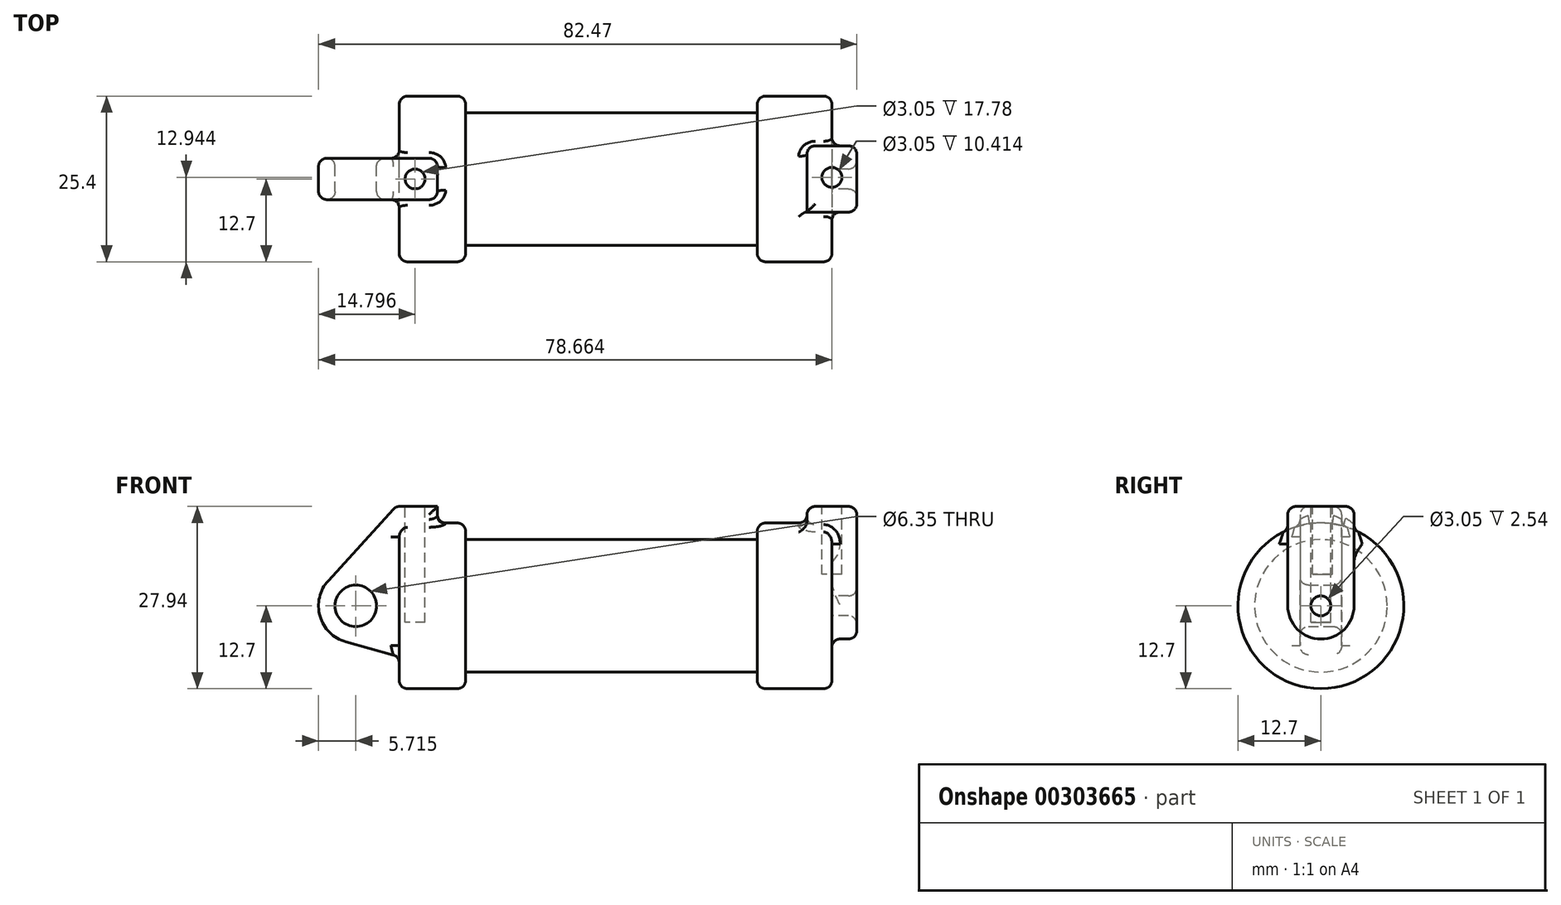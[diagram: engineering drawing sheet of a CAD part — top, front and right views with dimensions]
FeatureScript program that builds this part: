
annotation { "Feature Type Name" : "Feature", "Feature Type Description" : "" }
export const myFeature = defineFeature(function(context is Context, id is Id, definition is map)
    precondition{}
    {
        {
            var Q0;
            Q0=qCreatedBy(makeId("Front.planeOp"),FACE);
            var sketch = newSketch(context, id + "F0", { "sketchPlane" : qUnion([Q0])});
            skLineSegment(sketch, "E0", {"start": v(0, 0) * mm, "end": v(0, 12.7) * mm});
            skLineSegment(sketch, "E1", {"start": v(0, 12.7) * mm, "end": v(10.16, 12.7) * mm});
            skLineSegment(sketch, "E2", {"start": v(10.16, 12.7) * mm, "end": v(10.16, 10.16) * mm});
            skLineSegment(sketch, "E3", {"start": v(10.16, 10.16) * mm, "end": v(56.13, 10.16) * mm});
            skLineSegment(sketch, "E4", {"start": v(56.13, 10.16) * mm, "end": v(56.13, 12.7) * mm});
            skLineSegment(sketch, "E5", {"start": v(56.13, 12.7) * mm, "end": v(66.3, 12.7) * mm});
            skLineSegment(sketch, "E6", {"start": v(66.3, 12.7) * mm, "end": v(66.3, 0) * mm});
            skLineSegment(sketch, "E7", {"start": v(66.3, 0) * mm, "end": v(0, 0) * mm});
            skLineSegment(sketch, "E8", {"start": v(5.84, 15.24) * mm, "end": v(-0.5, 15.24) * mm});
            skLineSegment(sketch, "E9", {"start": v(-0.5, 15.24) * mm, "end": v(-10.88, 3.85) * mm});
            skLineSegment(sketch, "E10", {"start": v(0, 0) * mm, "end": v(-6.65, 0) * mm});
            skCircle(sketch, "E11", {"center": v(-6.65, 0) * mm, "radius": 5.72 * mm});
            skCircle(sketch, "E12", {"center": v(-6.65, 0) * mm, "radius": 3.18 * mm});
            skLineSegment(sketch, "E13", {"start": v(5.84, 15.24) * mm, "end": v(5.84, -9.4) * mm});
            skLineSegment(sketch, "E14", {"start": v(5.84, -9.4) * mm, "end": v(-8.18, -5.5) * mm});
            skCircle(sketch, "E15", {"center": v(-6.65, 0) * mm, "radius": 0.82 * mm});
            skSolve(sketch);
        }
        {
            var Q0;
            {var subQ0=sQuery(id+"F0.wireOp",EDGE,"E2");Q0=makeQuery(id+"F0.imprint","IMPRINT",FACE,{"disambiguationData":[TD([[makeQuery(id+"F0.imprint","IMPRINT",EDGE,{"derivedFrom":subQ0}),-1.0]])]});}
            var Q1;
            {var subQ0=sQuery(id+"F0.wireOp",EDGE,"E0");Q1=makeQuery(id+"F0.imprint","IMPRINT",FACE,{"disambiguationData":[TD([[makeQuery(id+"F0.imprint","IMPRINT",EDGE,{"derivedFrom":subQ0}),-1.0]])]});}
            var Q2;
            Q2=sQuery(id+"F0.wireOp",EDGE,"E7");
            revolve(context, id + "F1", {"entities" : qUnion([Q0, Q1]), "axis" : qUnion([Q2]), "revolveType" : RevolveType.FULL});
        }
        {
            var Q0;
            {var subQ0=sQuery(id+"F0.wireOp",EDGE,"E0");Q0=makeQuery(id+"F0.imprint","IMPRINT",FACE,{"disambiguationData":[TD([[makeQuery(id+"F0.imprint","IMPRINT",EDGE,{"derivedFrom":subQ0}),-1.0]])]});}
            var Q1;
            {var subQ1=sQuery(id+"F0.wireOp",EDGE,"E0");Q1=makeQuery(id+"F0.imprint","IMPRINT",FACE,{"disambiguationData":[TD([[makeQuery(id+"F0.imprint","IMPRINT",EDGE,{"derivedFrom":subQ1}),1.0]])]});}
            var Q2;
            {var subQ0=sQuery(id+"F0.wireOp",EDGE,"E14");Q2=makeQuery(id+"F0.imprint","IMPRINT",FACE,{"disambiguationData":[TD([[makeQuery(id+"F0.imprint","IMPRINT",EDGE,{"derivedFrom":subQ0}),-1.0]])]});}
            var Q3;
            Q3=makeQuery(id+"F0.imprint","IMPRINT",FACE,{"disambiguationData":[TD([[makeQuery(id+"F0.imprint","IMPRINT",EDGE,{"derivedFrom":sQuery(id+"F0.wireOp",EDGE,"E12")}),-1.0]])]});
            extrude(context, id + "F2", {"entities" : qUnion([Q0, Q1, Q2, Q3]), "operationType" : NewBodyOperationType.ADD, "endBound" : BoundingType.SYMMETRIC, "depth" : 6.35 * mm});
        }
        {
            var Q0;
            Q0=makeQuery(id+"F1.opRevolve","SWEPT_FACE",FACE,{"disambiguationData":[OSD([sQuery(id+"F0.wireOp",EDGE,"E6")])]});
            var sketch = newSketch(context, id + "F3", { "sketchPlane" : qUnion([Q0])});
            skCircle(sketch, "E16", {"center": v(0, 0) * mm, "radius": 5.08 * mm});
            skCircle(sketch, "E17", {"center": v(0, 0) * mm, "radius": 1.52 * mm});
            skLineSegment(sketch, "E18", {"start": v(-5.08, 0) * mm, "end": v(-5.08, 15.24) * mm});
            skLineSegment(sketch, "E19", {"start": v(5.08, 0) * mm, "end": v(5.08, 15.24) * mm});
            skLineSegment(sketch, "E20", {"start": v(-5.08, 15.24) * mm, "end": v(5.08, 15.24) * mm});
            skSolve(sketch);
        }
        {
            var Q0;
            Q0=makeQuery(id+"F1.opRevolve","SWEPT_FACE",FACE,{"disambiguationData":[OSD([sQuery(id+"F0.wireOp",EDGE,"E4")])]});
            extrude(context, id + "F4", {"entities" : qUnion([Q0]), "operationType" : NewBodyOperationType.ADD, "depth" : 1.27 * mm});
        }
        {
            var Q0;
            Q0=makeQuery(id+"F3.imprint","IMPRINT",FACE,{"disambiguationData":[TD([[makeQuery(id+"F3.imprint","IMPRINT",EDGE,{"derivedFrom":sQuery(id+"F3.wireOp",EDGE,"E17")}),-1.0]])]});
            var Q1;
            {var subQ0=sQuery(id+"F3.wireOp",EDGE,"E18");var subQ1=sQuery(id+"F3.wireOp",EDGE,"E16");var subQ2=makeQuery(id+"F3.imprint","INTERSECT",VERTEX,{"derivedFrom":[subQ1,subQ0]});Q1=makeQuery(id+"F3.imprint","IMPRINT",FACE,{"disambiguationData":[TD([[makeQuery(id+"F3.imprint","IMPRINT",EDGE,{"disambiguationData":[TD([[subQ2,1.0]])],"derivedFrom":subQ1}),-1.0]])]});}
            var Q2;
            {var subQ0=sQuery(id+"F3.wireOp",EDGE,"E20");Q2=makeQuery(id+"F3.imprint","IMPRINT",FACE,{"disambiguationData":[TD([[makeQuery(id+"F3.imprint","IMPRINT",EDGE,{"derivedFrom":subQ0}),-1.0]])]});}
            extrude(context, id + "F5", {"entities" : qUnion([Q0, Q1, Q2]), "operationType" : NewBodyOperationType.ADD, "endBound" : BoundingType.SYMMETRIC, "depth" : 7.62 * mm});
        }
        {
            var Q0;
            Q0=makeQuery(id+"F2.opExtrude","SWEPT_FACE",FACE,{"disambiguationData":[OSD([sQuery(id+"F0.wireOp",EDGE,"E8")])]});
            var sketch = newSketch(context, id + "F6", { "sketchPlane" : qUnion([Q0])});
            skCircle(sketch, "E21", {"center": v(2.43, 0) * mm, "radius": 1.52 * mm});
            skPoint(sketch, "E21.centerSnap0", {"position": v(-0.5, 0) * mm});
            skSolve(sketch);
        }
        {
            var Q0;
            Q0=makeQuery(id+"F5.opExtrude","SWEPT_FACE",FACE,{"disambiguationData":[OSD([sQuery(id+"F3.wireOp",EDGE,"E20")])]});
            var sketch = newSketch(context, id + "F7", { "sketchPlane" : qUnion([Q0])});
            skCircle(sketch, "E22", {"center": v(66.3, 0.24) * mm, "radius": 1.52 * mm});
            skPoint(sketch, "E22.centerSnap0", {"position": v(66.3, -5.08) * mm});
            skSolve(sketch);
        }
        {
            var Q0;
            Q0=makeQuery(id+"F6.imprint","IMPRINT",FACE,{"disambiguationData":[TD([[makeQuery(id+"F6.imprint","IMPRINT",EDGE,{"derivedFrom":sQuery(id+"F6.wireOp",EDGE,"E21")}),1.0]])]});
            extrude(context, id + "F8", {"entities" : qUnion([Q0]), "operationType" : NewBodyOperationType.REMOVE, "oppositeDirection" : true, "depth" : 17.78 * mm});
        }
        {
            var Q0;
            Q0=makeQuery(id+"F7.imprint","IMPRINT",FACE,{"disambiguationData":[TD([[makeQuery(id+"F7.imprint","IMPRINT",EDGE,{"derivedFrom":sQuery(id+"F7.wireOp",EDGE,"E22")}),1.0]])]});
            extrude(context, id + "F9", {"entities" : qUnion([Q0]), "operationType" : NewBodyOperationType.REMOVE, "oppositeDirection" : true, "depth" : 10.4 * mm});
        }
        {
            var Q0;
            Q0=makeQuery(id+"F1.opRevolve","SWEPT_FACE",FACE,{"disambiguationData":[OSD([sQuery(id+"F0.wireOp",EDGE,"E1")])]});
            var Q1;
            {var subQ0=sQuery(id+"F0.wireOp",EDGE,"E5");Q1=makeQuery(id+"F4.boolean.opBoolean","MERGE",FACE,{"derivedFrom":[makeQuery(id+"F1.opRevolve","SWEPT_FACE",FACE,{"disambiguationData":[OSD([subQ0])]}),makeQuery(id+"F4.opExtrude","SWEPT_FACE",FACE,{"disambiguationData":[OSD([sQuery(id+"F0.wireOp",EDGE,"E4"),subQ0])]})]});}
            var Q2;
            Q2=makeQuery(id+"F5.opExtrude","SWEPT_EDGE",EDGE,{"disambiguationData":[OSD([sQuery(id+"F3.wireOp",EDGE,"E18"),sQuery(id+"F3.wireOp",EDGE,"E20")])]});
            var Q3;
            Q3=makeQuery(id+"F5.opExtrude","CAP_EDGE",EDGE,{"disambiguationData":[OSD([sQuery(id+"F3.wireOp",EDGE,"E20")])],"isStart":true});
            var Q4;
            Q4=makeQuery(id+"F5.opExtrude","CAP_EDGE",EDGE,{"disambiguationData":[OSD([sQuery(id+"F3.wireOp",EDGE,"E19")])],"isStart":true});
            var Q5;
            Q5=makeQuery(id+"F5.opExtrude","SWEPT_EDGE",EDGE,{"disambiguationData":[OSD([sQuery(id+"F3.wireOp",EDGE,"E19"),sQuery(id+"F3.wireOp",EDGE,"E20")])]});
            var Q6;
            Q6=makeQuery(id+"F5.opExtrude","CAP_EDGE",EDGE,{"disambiguationData":[OSD([sQuery(id+"F3.wireOp",EDGE,"E20")])],"isStart":false});
            var Q7;
            Q7=makeQuery(id+"F2.opExtrude","CAP_EDGE",EDGE,{"disambiguationData":[OSD([sQuery(id+"F0.wireOp",EDGE,"E13")])],"isStart":false});
            var Q8;
            Q8=makeQuery(id+"F2.opExtrude","CAP_EDGE",EDGE,{"disambiguationData":[OSD([sQuery(id+"F0.wireOp",EDGE,"E8")])],"isStart":true});
            var Q9;
            Q9=makeQuery(id+"F2.opExtrude","CAP_FACE",FACE,{"disambiguationData":[OSD([sQuery(id+"F0.wireOp",EDGE,"E8"),sQuery(id+"F0.wireOp",EDGE,"E9"),sQuery(id+"F0.wireOp",EDGE,"E11"),sQuery(id+"F0.wireOp",EDGE,"E12"),sQuery(id+"F0.wireOp",EDGE,"E13"),sQuery(id+"F0.wireOp",EDGE,"E14")])],"isStart":true});
            var Q10;
            Q10=makeQuery(id+"F2.opExtrude","SWEPT_FACE",FACE,{"disambiguationData":[OSD([sQuery(id+"F0.wireOp",EDGE,"E9")])]});
            var Q11;
            Q11=makeQuery(id+"F2.opExtrude","CAP_FACE",FACE,{"disambiguationData":[OSD([sQuery(id+"F0.wireOp",EDGE,"E8"),sQuery(id+"F0.wireOp",EDGE,"E9"),sQuery(id+"F0.wireOp",EDGE,"E11"),sQuery(id+"F0.wireOp",EDGE,"E12"),sQuery(id+"F0.wireOp",EDGE,"E13"),sQuery(id+"F0.wireOp",EDGE,"E14")])],"isStart":false});
            var Q12;
            Q12=makeQuery(id+"F2.boolean.opBoolean","INTERSECT",EDGE,{"derivedFrom":[makeQuery(id+"F1.opRevolve","SWEPT_FACE",FACE,{"disambiguationData":[OSD([sQuery(id+"F0.wireOp",EDGE,"E0")])]}),makeQuery(id+"F2.opExtrude","SWEPT_FACE",FACE,{"disambiguationData":[OSD([sQuery(id+"F0.wireOp",EDGE,"E14")])]})]});
            var Q13;
            Q13=makeQuery(id+"F2.opExtrude","SWEPT_EDGE",EDGE,{"disambiguationData":[OSD([sQuery(id+"F0.wireOp",EDGE,"E11"),sQuery(id+"F0.wireOp",EDGE,"E14")])]});
            var Q14;
            Q14=makeQuery(id+"F5.opExtrude","CAP_FACE",FACE,{"disambiguationData":[OSD([sQuery(id+"F3.wireOp",EDGE,"E16"),sQuery(id+"F3.wireOp",EDGE,"E17"),sQuery(id+"F3.wireOp",EDGE,"E18"),sQuery(id+"F3.wireOp",EDGE,"E19"),sQuery(id+"F3.wireOp",EDGE,"E20")])],"isStart":false});
            var Q15;
            Q15=makeQuery(id+"F5.boolean.opBoolean","INTERSECT",EDGE,{"derivedFrom":[makeQuery(id+"F1.opRevolve","SWEPT_FACE",FACE,{"disambiguationData":[OSD([sQuery(id+"F0.wireOp",EDGE,"E6")])]}),makeQuery(id+"F5.opExtrude","SWEPT_FACE",FACE,{"disambiguationData":[OSD([sQuery(id+"F3.wireOp",EDGE,"E16")])]})]});
            var Q16;
            Q16=makeQuery(id+"F5.boolean.opBoolean","INTERSECT",EDGE,{"derivedFrom":[makeQuery(id+"F1.opRevolve","SWEPT_FACE",FACE,{"disambiguationData":[OSD([sQuery(id+"F0.wireOp",EDGE,"E6")])]}),makeQuery(id+"F5.opExtrude","SWEPT_FACE",FACE,{"disambiguationData":[OSD([sQuery(id+"F3.wireOp",EDGE,"E18")])]})]});
            fillet(context, id + "F10", {"entities" : qUnion([Q0, Q1, Q2, Q3, Q4, Q5, Q6, Q7, Q8, Q9, Q10, Q11, Q12, Q13, Q14, Q15, Q16]), "radius" : 1.27 * mm, "allowEdgeOverflow" : false});
        }
    });
